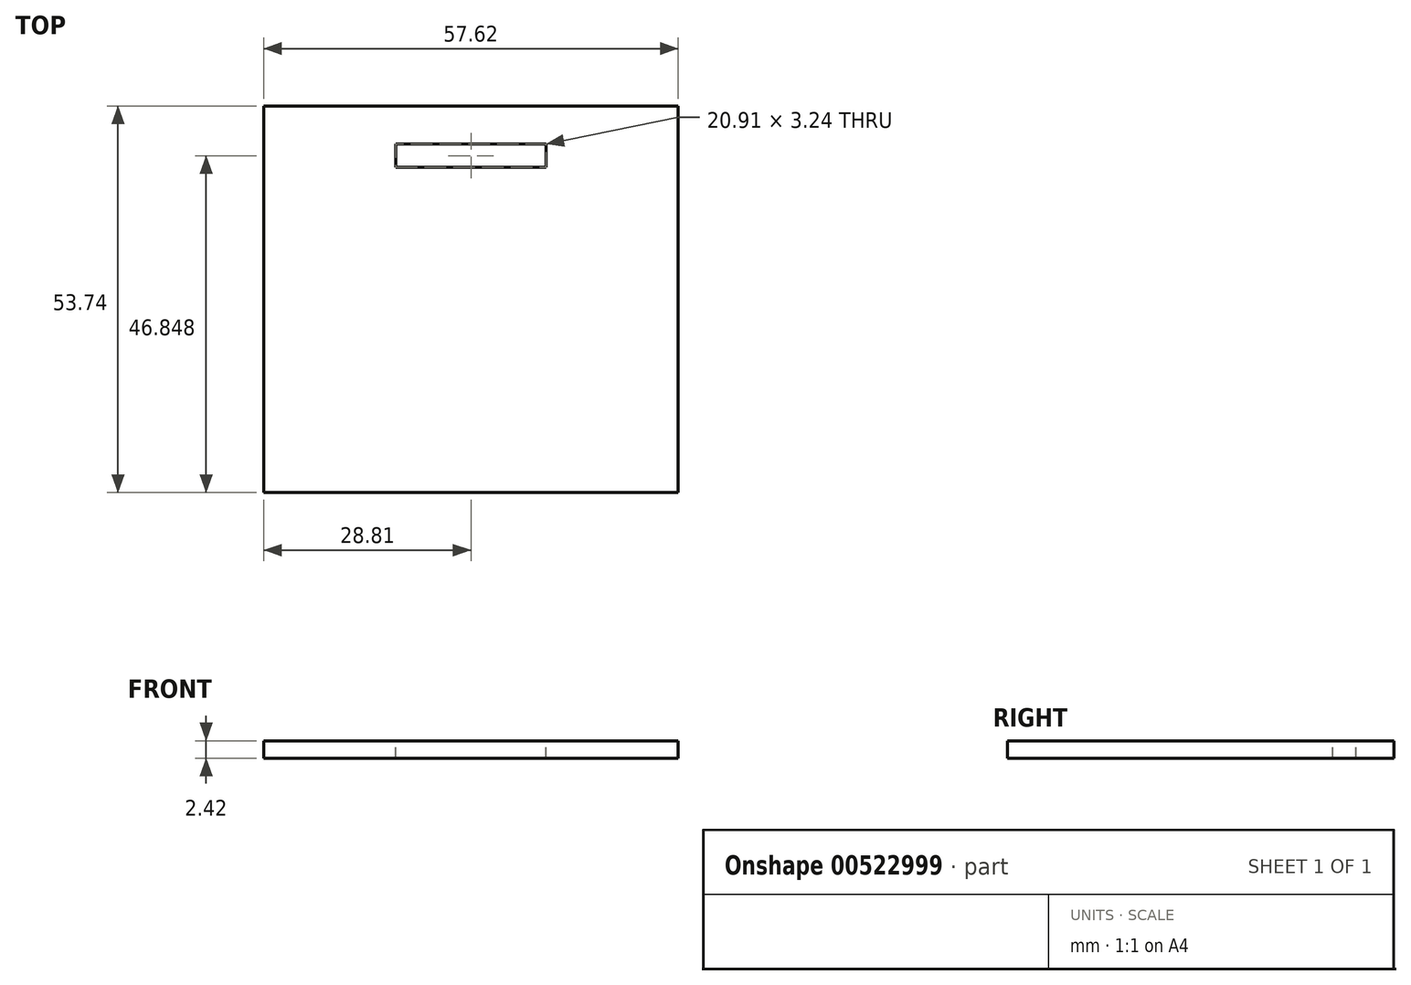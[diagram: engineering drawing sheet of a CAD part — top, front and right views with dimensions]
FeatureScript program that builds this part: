
annotation { "Feature Type Name" : "Feature", "Feature Type Description" : "" }
export const myFeature = defineFeature(function(context is Context, id is Id, definition is map)
    precondition{}
    {
        {
            var Q0;
            Q0=qCreatedBy(makeId("Front.planeOp"),FACE);
            var sketch = newSketch(context, id + "F0", { "sketchPlane" : qUnion([Q0])});
            skLineSegment(sketch, "E0.bottom", {"start": v(34.1, -59.67) * mm, "end": v(-34.1, -59.67) * mm});
            skLineSegment(sketch, "E0.top", {"start": v(34.1, 129.65) * mm, "end": v(-34.1, 129.65) * mm});
            skLineSegment(sketch, "E0.left", {"start": v(34.1, -59.67) * mm, "end": v(34.1, 129.65) * mm});
            skLineSegment(sketch, "E0.right", {"start": v(-34.1, -59.67) * mm, "end": v(-34.1, 129.65) * mm});
            skPoint(sketch, "E0.middle", {"position": v(0, 34.99) * mm});
            skSolve(sketch);
        }
        {
            var Q0;
            Q0=makeQuery(id+"F0.imprint","IMPRINT",FACE,{"disambiguationData":[TD([[makeQuery(id+"F0.imprint","IMPRINT",EDGE,{"derivedFrom":sQuery(id+"F0.wireOp",EDGE,"E0.bottom")}),-1.0]])]});
            var sketch = newSketch(context, id + "F1", { "sketchPlane" : qUnion([Q0])});
            skLineSegment(sketch, "E1.bottom", {"start": v(28.81, 113.16) * mm, "end": v(-28.81, 113.16) * mm});
            skLineSegment(sketch, "E1.top", {"start": v(28.81, 115.58) * mm, "end": v(-28.81, 115.58) * mm});
            skLineSegment(sketch, "E1.left", {"start": v(28.81, 113.16) * mm, "end": v(28.81, 115.58) * mm});
            skLineSegment(sketch, "E1.right", {"start": v(-28.81, 113.16) * mm, "end": v(-28.81, 115.58) * mm});
            skPoint(sketch, "E1.middle", {"position": v(0, 114.37) * mm});
            skSolve(sketch);
        }
        {
            var Q0;
            Q0 = qSketchRegion(id + "F1", true);
            extrude(context, id + "F2", {"entities" : qUnion([Q0]), "depth" : 53.74 * mm, "offsetDistance" : 25 * mm});
        }
        {
            var Q0;
            Q0=makeQuery(id+"F2.opExtrude","SWEPT_FACE",FACE,{"disambiguationData":[OSD([sQuery(id+"F1.wireOp",EDGE,"E1.top")])]});
            var sketch = newSketch(context, id + "F3", { "sketchPlane" : qUnion([Q0])});
            skLineSegment(sketch, "E2.bottom", {"start": v(10.45, -8.51) * mm, "end": v(-10.45, -8.51) * mm});
            skLineSegment(sketch, "E2.top", {"start": v(10.45, -5.27) * mm, "end": v(-10.45, -5.27) * mm});
            skLineSegment(sketch, "E2.left", {"start": v(10.45, -8.51) * mm, "end": v(10.45, -5.27) * mm});
            skLineSegment(sketch, "E2.right", {"start": v(-10.45, -8.51) * mm, "end": v(-10.45, -5.27) * mm});
            skPoint(sketch, "E2.middle", {"position": v(0, -6.9) * mm});
            skSolve(sketch);
        }
        {
            var Q0;
            Q0 = qSketchRegion(id + "F3", true);
            extrude(context, id + "F4", {"entities" : qUnion([Q0]), "operationType" : NewBodyOperationType.REMOVE, "oppositeDirection" : true, "depth" : 25 * mm, "offsetDistance" : 25 * mm});
        }
        {
            var Q0;
            Q0=makeQuery(id+"F1.imprint","IMPRINT",FACE,{"disambiguationData":[TD([[makeQuery(id+"F1.imprint","IMPRINT",EDGE,{"derivedFrom":sQuery(id+"F1.wireOp",EDGE,"E1.bottom")}),1.0]])]});
            var sketch = newSketch(context, id + "F5", { "sketchPlane" : qUnion([Q0])});
            skLineSegment(sketch, "E3.bottom", {"start": v(-19.7, -9.4) * mm, "end": v(19.7, -9.4) * mm});
            skLineSegment(sketch, "E3.top", {"start": v(-19.7, -1.17) * mm, "end": v(19.7, -1.17) * mm});
            skLineSegment(sketch, "E3.left", {"start": v(-19.7, -9.4) * mm, "end": v(-19.7, -1.17) * mm});
            skLineSegment(sketch, "E3.right", {"start": v(19.7, -9.4) * mm, "end": v(19.7, -1.17) * mm});
            skPoint(sketch, "E3.middle", {"position": v(0, -5.29) * mm});
            skSolve(sketch);
        }
        {
            var Q0;
            Q0 = qSketchRegion(id + "F5", true);
            extrude(context, id + "F6", {"entities" : qUnion([Q0]), "operationType" : NewBodyOperationType.REMOVE, "depth" : 25 * mm, "offsetDistance" : 25 * mm});
        }
    });
